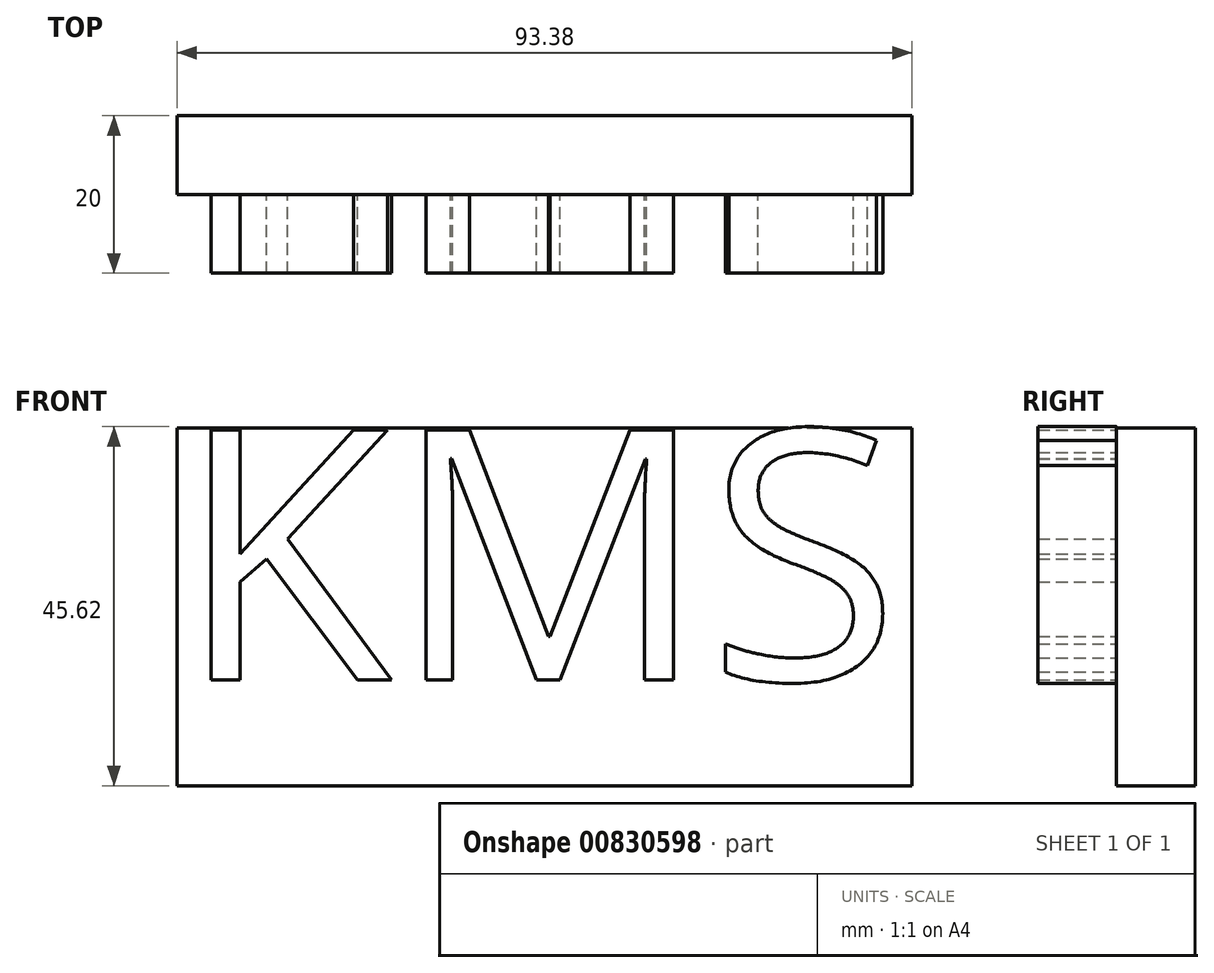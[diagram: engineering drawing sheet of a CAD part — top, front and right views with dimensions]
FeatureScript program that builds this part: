
annotation { "Feature Type Name" : "Feature", "Feature Type Description" : "" }
export const myFeature = defineFeature(function(context is Context, id is Id, definition is map)
    precondition{}
    {
        {
            var Q0;
            Q0=qCreatedBy(makeId("Front.planeOp"),FACE);
            var sketch = newSketch(context, id + "F0", { "sketchPlane" : qUnion([Q0])});
            skLineSegment(sketch, "E0.bottom", {"start": v(0, 0) * mm, "end": v(93.38, 0) * mm});
            skLineSegment(sketch, "E0.top", {"start": v(0, 45.44) * mm, "end": v(93.38, 45.44) * mm});
            skLineSegment(sketch, "E0.left", {"start": v(0, 0) * mm, "end": v(0, 45.44) * mm});
            skLineSegment(sketch, "E0.right", {"start": v(93.38, 0) * mm, "end": v(93.38, 45.44) * mm});
            skSolve(sketch);
        }
        {
            var Q0;
            Q0=makeQuery(id+"F0.imprint","IMPRINT",FACE,{"disambiguationData":[TD([[makeQuery(id+"F0.imprint","IMPRINT",EDGE,{"derivedFrom":sQuery(id+"F0.wireOp",EDGE,"E0.bottom")}),1.0]])]});
            extrude(context, id + "F1", {"entities" : qUnion([Q0]), "depth" : 10 * mm, "offsetDistance" : 25.4 * mm});
        }
        {
            var Q0;
            Q0=makeQuery(id+"F1.opExtrude","CAP_FACE",FACE,{"disambiguationData":[OSD([sQuery(id+"F0.wireOp",EDGE,"E0.bottom"),sQuery(id+"F0.wireOp",EDGE,"E0.top"),sQuery(id+"F0.wireOp",EDGE,"E0.left"),sQuery(id+"F0.wireOp",EDGE,"E0.right")])],"isStart":false});
            var sketch = newSketch(context, id + "F2", { "sketchPlane" : qUnion([Q0])});
            skText(sketch, "E1", { "text": "KMS", "fontName": "OpenSans-Regular.ttf"});
            const initialGuessF2  = {"E1": [0, 0.01344, 1, 0, 0.032]};
            skSetInitialGuess(sketch, initialGuessF2);
            skSolve(sketch);
        }
        {
            var Q0;
            Q0 = qSketchRegion(id + "F2", true);
            extrude(context, id + "F3", {"entities" : qUnion([Q0]), "operationType" : NewBodyOperationType.ADD, "depth" : 10 * mm, "offsetDistance" : 25.4 * mm});
        }
    });
